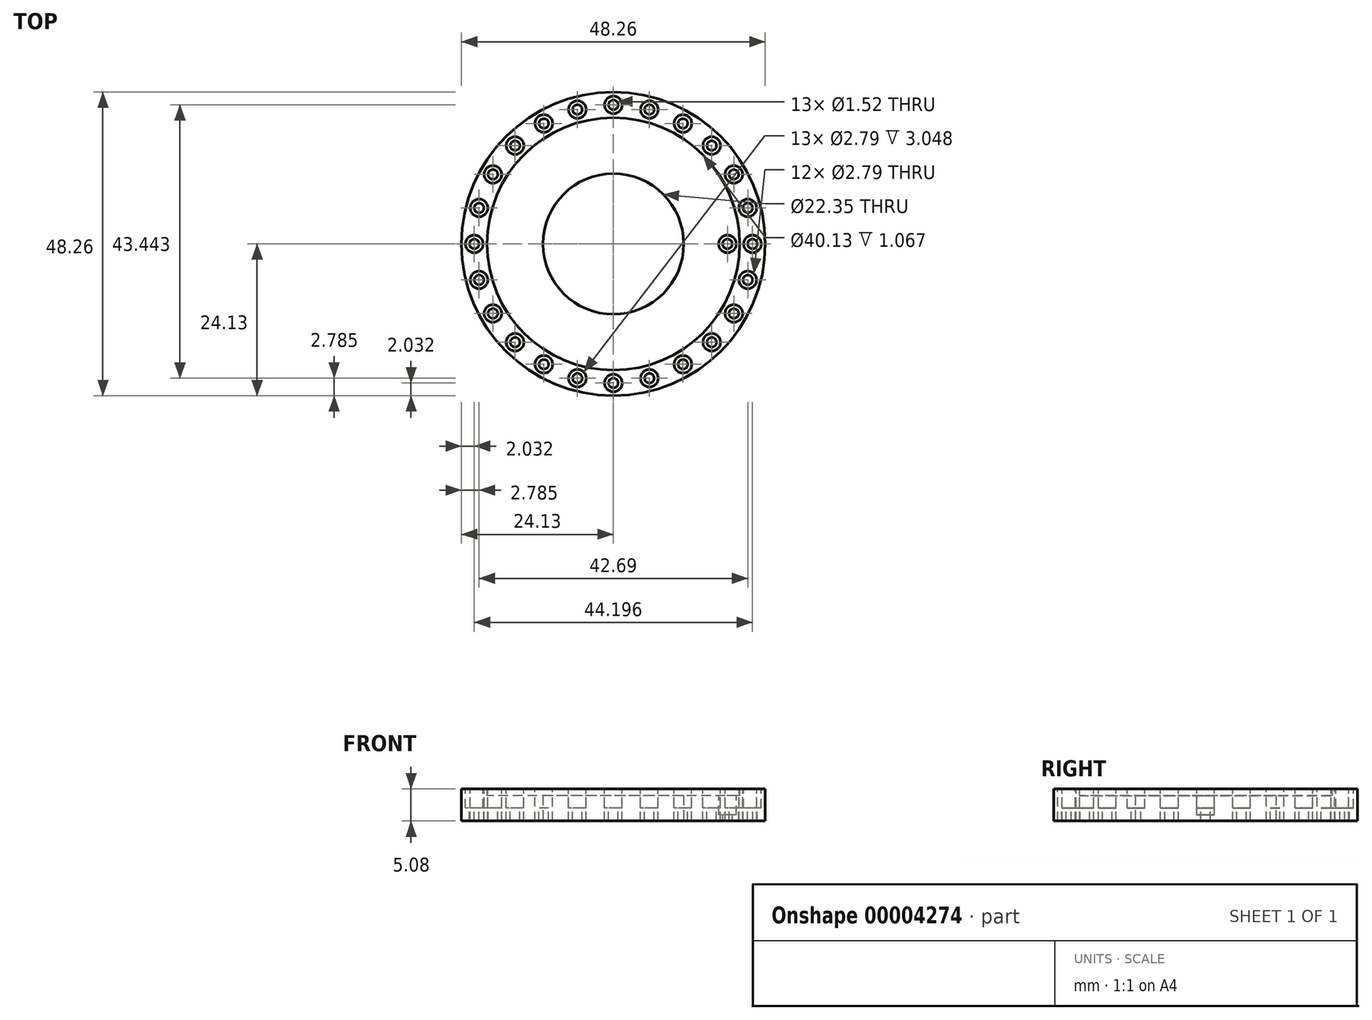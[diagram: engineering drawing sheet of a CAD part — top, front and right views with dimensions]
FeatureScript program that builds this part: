
annotation { "Feature Type Name" : "Feature", "Feature Type Description" : "" }
export const myFeature = defineFeature(function(context is Context, id is Id, definition is map)
    precondition{}
    {
        {
            var Q0;
            Q0=qCreatedBy(makeId("Top.planeOp"),FACE);
            var sketch = newSketch(context, id + "F0", { "sketchPlane" : qUnion([Q0])});
            skCircle(sketch, "E0", {"center": v(0, 0) * mm, "radius": 24.13 * mm});
            skCircle(sketch, "E1", {"center": v(0, 0) * mm, "radius": 20.07 * mm});
            skCircle(sketch, "E2", {"center": v(0, 0) * mm, "radius": 11.18 * mm});
            skSolve(sketch);
        }
        {
            var Q0;
            Q0=makeQuery(id+"F0.imprint","IMPRINT",FACE,{"disambiguationData":[TD([[makeQuery(id+"F0.imprint","IMPRINT",EDGE,{"derivedFrom":sQuery(id+"F0.wireOp",EDGE,"E1")}),1.0]])]});
            extrude(context, id + "F1", {"entities" : qUnion([Q0]), "depth" : 4 * mm});
        }
        {
            var Q0;
            Q0=makeQuery(id+"F0.imprint","IMPRINT",FACE,{"disambiguationData":[TD([[makeQuery(id+"F0.imprint","IMPRINT",EDGE,{"derivedFrom":sQuery(id+"F0.wireOp",EDGE,"E0")}),1.0]])]});
            extrude(context, id + "F2", {"entities" : qUnion([Q0]), "operationType" : NewBodyOperationType.ADD, "depth" : 5.08 * mm});
        }
        {
            var Q0;
            Q0=makeQuery(id+"F1.opExtrude","CAP_FACE",FACE,{"disambiguationData":[OSD([sQuery(id+"F0.wireOp",EDGE,"E1"),sQuery(id+"F0.wireOp",EDGE,"E2")])],"isStart":false});
            var sketch = newSketch(context, id + "F3", { "sketchPlane" : qUnion([Q0])});
            skLineSegment(sketch, "E3", {"start": v(0, 0) * mm, "end": v(16.71, 0) * mm});
            skCircle(sketch, "E4", {"center": v(18.11, 0) * mm, "radius": 0.76 * mm});
            skLineSegment(sketch, "E5.trimOffspring", {"start": v(19.5, 0) * mm, "end": v(20.07, 0) * mm});
            skCircle(sketch, "E6", {"center": v(18.11, 0) * mm, "radius": 1.4 * mm});
            skSolve(sketch);
        }
        {
            var Q0;
            {var subQ0=sQuery(id+"F3.wireOp",EDGE,"E4");var subQ2=makeQuery(id+"F3.imprint","INTERSECT",VERTEX,{"derivedFrom":[sQuery(id+"F3.wireOp",EDGE,"E3"),subQ0]});Q0=makeQuery(id+"F3.imprint","IMPRINT",FACE,{"disambiguationData":[TD([[makeQuery(id+"F3.imprint","IMPRINT",EDGE,{"disambiguationData":[TD([[subQ2,1.0]])],"derivedFrom":subQ0}),1.0]])]});}
            extrude(context, id + "F4", {"entities" : qUnion([Q0]), "operationType" : NewBodyOperationType.REMOVE, "endBound" : BoundingType.THROUGH_ALL, "oppositeDirection" : true, "depth" : 2.8 * mm});
        }
        {
            var Q0;
            Q0=makeQuery(id+"F2.opExtrude","CAP_FACE",FACE,{"disambiguationData":[OSD([sQuery(id+"F0.wireOp",EDGE,"E0"),sQuery(id+"F0.wireOp",EDGE,"E1")])],"isStart":false});
            var sketch = newSketch(context, id + "F5", { "sketchPlane" : qUnion([Q0])});
            skLineSegment(sketch, "E7", {"start": v(0, 0) * mm, "end": v(21.34, 0) * mm, "construction": true});
            skLineSegment(sketch, "E8", {"start": v(0, 0) * mm, "end": v(20.6, 5.52) * mm, "construction": true});
            skCircle(sketch, "E9", {"center": v(22.1, 0) * mm, "radius": 0.76 * mm});
            skCircle(sketch, "E10", {"center": v(21.35, 5.72) * mm, "radius": 0.76 * mm});
            skCircle(sketch, "E11.0.MirrorC", {"center": v(19.14, 11.05) * mm, "radius": 0.76 * mm});
            skLineSegment(sketch, "E12", {"start": v(0, 0) * mm, "end": v(18.48, 10.67) * mm, "construction": true});
            skCircle(sketch, "E13.0.MirrorC", {"center": v(15.63, 15.63) * mm, "radius": 0.76 * mm});
            skCircle(sketch, "E14.0.MirrorC", {"center": v(11.05, 19.14) * mm, "radius": 0.76 * mm});
            skLineSegment(sketch, "E15", {"start": v(0, 0) * mm, "end": v(10.67, 18.48) * mm, "construction": true});
            skCircle(sketch, "E16.0.MirrorC", {"center": v(5.72, 21.35) * mm, "radius": 0.76 * mm});
            skCircle(sketch, "E17.0.MirrorC", {"center": v(0, 22.1) * mm, "radius": 0.76 * mm});
            skCircle(sketch, "E18.0.MirrorC", {"center": v(-5.72, 21.35) * mm, "radius": 0.76 * mm});
            skCircle(sketch, "E19.0.MirrorC", {"center": v(-11.05, 19.14) * mm, "radius": 0.76 * mm});
            skLineSegment(sketch, "E20", {"start": v(0, 0) * mm, "end": v(-10.67, 18.48) * mm, "construction": true});
            skCircle(sketch, "E21.0.MirrorC", {"center": v(-15.63, 15.63) * mm, "radius": 0.76 * mm});
            skCircle(sketch, "E22.0.MirrorC", {"center": v(-19.14, 11.05) * mm, "radius": 0.76 * mm});
            skCircle(sketch, "E23.0.MirrorC", {"center": v(-21.35, 5.72) * mm, "radius": 0.76 * mm});
            skCircle(sketch, "E24.0.MirrorC", {"center": v(-22.1, 0) * mm, "radius": 0.76 * mm});
            skCircle(sketch, "E25.0.MirrorC", {"center": v(-21.35, -5.72) * mm, "radius": 0.76 * mm});
            skCircle(sketch, "E26.0.MirrorC", {"center": v(-19.14, -11.05) * mm, "radius": 0.76 * mm});
            skCircle(sketch, "E27.0.MirrorC", {"center": v(-15.63, -15.63) * mm, "radius": 0.76 * mm});
            skCircle(sketch, "E28.0.MirrorC", {"center": v(-11.05, -19.14) * mm, "radius": 0.76 * mm});
            skCircle(sketch, "E29.0.MirrorC", {"center": v(21.35, -5.72) * mm, "radius": 0.76 * mm});
            skCircle(sketch, "E30.0.MirrorC", {"center": v(19.14, -11.05) * mm, "radius": 0.76 * mm});
            skCircle(sketch, "E31.0.MirrorC", {"center": v(15.63, -15.63) * mm, "radius": 0.76 * mm});
            skCircle(sketch, "E32.0.MirrorC", {"center": v(11.05, -19.14) * mm, "radius": 0.76 * mm});
            skCircle(sketch, "E33.0.MirrorC", {"center": v(5.72, -21.35) * mm, "radius": 0.76 * mm});
            skCircle(sketch, "E34.0.MirrorC", {"center": v(0, -22.1) * mm, "radius": 0.76 * mm});
            skCircle(sketch, "E35.0.MirrorC", {"center": v(-5.72, -21.35) * mm, "radius": 0.76 * mm});
            skLineSegment(sketch, "E36.trimOffspring", {"start": v(22.08, 5.92) * mm, "end": v(23.3, 6.25) * mm, "construction": true});
            skLineSegment(sketch, "E37.trimOffspring", {"start": v(22.86, 0) * mm, "end": v(24.13, 0) * mm, "construction": true});
            skCircle(sketch, "E38", {"center": v(22.1, 0) * mm, "radius": 1.4 * mm});
            skCircle(sketch, "E39", {"center": v(21.35, 5.72) * mm, "radius": 1.4 * mm});
            skCircle(sketch, "E40", {"center": v(19.14, 11.05) * mm, "radius": 1.4 * mm});
            skCircle(sketch, "E41", {"center": v(15.63, 15.63) * mm, "radius": 1.4 * mm});
            skCircle(sketch, "E42", {"center": v(11.05, 19.14) * mm, "radius": 1.4 * mm});
            skCircle(sketch, "E43", {"center": v(5.72, 21.35) * mm, "radius": 1.4 * mm});
            skCircle(sketch, "E44", {"center": v(0, 22.1) * mm, "radius": 1.4 * mm});
            skCircle(sketch, "E45", {"center": v(-5.72, 21.35) * mm, "radius": 1.4 * mm});
            skCircle(sketch, "E46", {"center": v(-11.05, 19.14) * mm, "radius": 1.4 * mm});
            skCircle(sketch, "E47", {"center": v(-15.63, 15.63) * mm, "radius": 1.4 * mm});
            skCircle(sketch, "E48", {"center": v(-19.14, 11.05) * mm, "radius": 1.4 * mm});
            skCircle(sketch, "E49", {"center": v(-21.35, 5.72) * mm, "radius": 1.4 * mm});
            skCircle(sketch, "E50", {"center": v(-22.1, 0) * mm, "radius": 1.4 * mm});
            skCircle(sketch, "E51", {"center": v(-21.35, -5.72) * mm, "radius": 1.4 * mm});
            skCircle(sketch, "E52", {"center": v(-19.14, -11.05) * mm, "radius": 1.4 * mm});
            skCircle(sketch, "E53", {"center": v(-15.63, -15.63) * mm, "radius": 1.4 * mm});
            skCircle(sketch, "E54", {"center": v(-11.05, -19.14) * mm, "radius": 1.4 * mm});
            skCircle(sketch, "E55", {"center": v(-5.72, -21.35) * mm, "radius": 1.4 * mm});
            skCircle(sketch, "E56", {"center": v(0, -22.1) * mm, "radius": 1.4 * mm});
            skCircle(sketch, "E57", {"center": v(5.72, -21.35) * mm, "radius": 1.4 * mm});
            skCircle(sketch, "E58", {"center": v(11.05, -19.14) * mm, "radius": 1.4 * mm});
            skCircle(sketch, "E59", {"center": v(15.63, -15.63) * mm, "radius": 1.4 * mm});
            skCircle(sketch, "E60", {"center": v(19.14, -11.05) * mm, "radius": 1.4 * mm});
            skCircle(sketch, "E61", {"center": v(21.35, -5.72) * mm, "radius": 1.4 * mm});
            skSolve(sketch);
        }
        {
            var Q0;
            Q0=makeQuery(id+"F5.imprint","IMPRINT",FACE,{"disambiguationData":[TD([[makeQuery(id+"F5.imprint","IMPRINT",EDGE,{"derivedFrom":sQuery(id+"F5.wireOp",EDGE,"E9")}),1.0]])]});
            var Q1;
            Q1=makeQuery(id+"F5.imprint","IMPRINT",FACE,{"disambiguationData":[TD([[makeQuery(id+"F5.imprint","IMPRINT",EDGE,{"derivedFrom":sQuery(id+"F5.wireOp",EDGE,"E10")}),1.0]])]});
            var Q2;
            Q2=makeQuery(id+"F5.imprint","IMPRINT",FACE,{"disambiguationData":[TD([[makeQuery(id+"F5.imprint","IMPRINT",EDGE,{"derivedFrom":sQuery(id+"F5.wireOp",EDGE,"E11.0.MirrorC")}),-1.0]])]});
            var Q3;
            Q3=makeQuery(id+"F5.imprint","IMPRINT",FACE,{"disambiguationData":[TD([[makeQuery(id+"F5.imprint","IMPRINT",EDGE,{"derivedFrom":sQuery(id+"F5.wireOp",EDGE,"E13.0.MirrorC")}),-1.0]])]});
            var Q4;
            Q4=makeQuery(id+"F5.imprint","IMPRINT",FACE,{"disambiguationData":[TD([[makeQuery(id+"F5.imprint","IMPRINT",EDGE,{"derivedFrom":sQuery(id+"F5.wireOp",EDGE,"E14.0.MirrorC")}),-1.0]])]});
            var Q5;
            Q5=makeQuery(id+"F5.imprint","IMPRINT",FACE,{"disambiguationData":[TD([[makeQuery(id+"F5.imprint","IMPRINT",EDGE,{"derivedFrom":sQuery(id+"F5.wireOp",EDGE,"E16.0.MirrorC")}),1.0]])]});
            var Q6;
            Q6=makeQuery(id+"F5.imprint","IMPRINT",FACE,{"disambiguationData":[TD([[makeQuery(id+"F5.imprint","IMPRINT",EDGE,{"derivedFrom":sQuery(id+"F5.wireOp",EDGE,"E17.0.MirrorC")}),1.0]])]});
            var Q7;
            Q7=makeQuery(id+"F5.imprint","IMPRINT",FACE,{"disambiguationData":[TD([[makeQuery(id+"F5.imprint","IMPRINT",EDGE,{"derivedFrom":sQuery(id+"F5.wireOp",EDGE,"E18.0.MirrorC")}),-1.0]])]});
            var Q8;
            Q8=makeQuery(id+"F5.imprint","IMPRINT",FACE,{"disambiguationData":[TD([[makeQuery(id+"F5.imprint","IMPRINT",EDGE,{"derivedFrom":sQuery(id+"F5.wireOp",EDGE,"E19.0.MirrorC")}),-1.0]])]});
            var Q9;
            Q9=makeQuery(id+"F5.imprint","IMPRINT",FACE,{"disambiguationData":[TD([[makeQuery(id+"F5.imprint","IMPRINT",EDGE,{"derivedFrom":sQuery(id+"F5.wireOp",EDGE,"E21.0.MirrorC")}),1.0]])]});
            var Q10;
            Q10=makeQuery(id+"F5.imprint","IMPRINT",FACE,{"disambiguationData":[TD([[makeQuery(id+"F5.imprint","IMPRINT",EDGE,{"derivedFrom":sQuery(id+"F5.wireOp",EDGE,"E22.0.MirrorC")}),-1.0]])]});
            var Q11;
            Q11=makeQuery(id+"F5.imprint","IMPRINT",FACE,{"disambiguationData":[TD([[makeQuery(id+"F5.imprint","IMPRINT",EDGE,{"derivedFrom":sQuery(id+"F5.wireOp",EDGE,"E23.0.MirrorC")}),-1.0]])]});
            var Q12;
            Q12=makeQuery(id+"F5.imprint","IMPRINT",FACE,{"disambiguationData":[TD([[makeQuery(id+"F5.imprint","IMPRINT",EDGE,{"derivedFrom":sQuery(id+"F5.wireOp",EDGE,"E24.0.MirrorC")}),1.0]])]});
            var Q13;
            Q13=makeQuery(id+"F5.imprint","IMPRINT",FACE,{"disambiguationData":[TD([[makeQuery(id+"F5.imprint","IMPRINT",EDGE,{"derivedFrom":sQuery(id+"F5.wireOp",EDGE,"E25.0.MirrorC")}),1.0]])]});
            var Q14;
            Q14=makeQuery(id+"F5.imprint","IMPRINT",FACE,{"disambiguationData":[TD([[makeQuery(id+"F5.imprint","IMPRINT",EDGE,{"derivedFrom":sQuery(id+"F5.wireOp",EDGE,"E26.0.MirrorC")}),1.0]])]});
            var Q15;
            Q15=makeQuery(id+"F5.imprint","IMPRINT",FACE,{"disambiguationData":[TD([[makeQuery(id+"F5.imprint","IMPRINT",EDGE,{"derivedFrom":sQuery(id+"F5.wireOp",EDGE,"E27.0.MirrorC")}),-1.0]])]});
            var Q16;
            Q16=makeQuery(id+"F5.imprint","IMPRINT",FACE,{"disambiguationData":[TD([[makeQuery(id+"F5.imprint","IMPRINT",EDGE,{"derivedFrom":sQuery(id+"F5.wireOp",EDGE,"E28.0.MirrorC")}),-1.0]])]});
            var Q17;
            Q17=makeQuery(id+"F5.imprint","IMPRINT",FACE,{"disambiguationData":[TD([[makeQuery(id+"F5.imprint","IMPRINT",EDGE,{"derivedFrom":sQuery(id+"F5.wireOp",EDGE,"E35.0.MirrorC")}),1.0]])]});
            var Q18;
            Q18=makeQuery(id+"F5.imprint","IMPRINT",FACE,{"disambiguationData":[TD([[makeQuery(id+"F5.imprint","IMPRINT",EDGE,{"derivedFrom":sQuery(id+"F5.wireOp",EDGE,"E34.0.MirrorC")}),-1.0]])]});
            var Q19;
            Q19=makeQuery(id+"F5.imprint","IMPRINT",FACE,{"disambiguationData":[TD([[makeQuery(id+"F5.imprint","IMPRINT",EDGE,{"derivedFrom":sQuery(id+"F5.wireOp",EDGE,"E33.0.MirrorC")}),-1.0]])]});
            var Q20;
            Q20=makeQuery(id+"F5.imprint","IMPRINT",FACE,{"disambiguationData":[TD([[makeQuery(id+"F5.imprint","IMPRINT",EDGE,{"derivedFrom":sQuery(id+"F5.wireOp",EDGE,"E32.0.MirrorC")}),1.0]])]});
            var Q21;
            Q21=makeQuery(id+"F5.imprint","IMPRINT",FACE,{"disambiguationData":[TD([[makeQuery(id+"F5.imprint","IMPRINT",EDGE,{"derivedFrom":sQuery(id+"F5.wireOp",EDGE,"E31.0.MirrorC")}),1.0]])]});
            var Q22;
            Q22=makeQuery(id+"F5.imprint","IMPRINT",FACE,{"disambiguationData":[TD([[makeQuery(id+"F5.imprint","IMPRINT",EDGE,{"derivedFrom":sQuery(id+"F5.wireOp",EDGE,"E30.0.MirrorC")}),1.0]])]});
            var Q23;
            Q23=makeQuery(id+"F5.imprint","IMPRINT",FACE,{"disambiguationData":[TD([[makeQuery(id+"F5.imprint","IMPRINT",EDGE,{"derivedFrom":sQuery(id+"F5.wireOp",EDGE,"E29.0.MirrorC")}),-1.0]])]});
            extrude(context, id + "F6", {"entities" : qUnion([Q0, Q1, Q2, Q3, Q4, Q5, Q6, Q7, Q8, Q9, Q10, Q11, Q12, Q13, Q14, Q15, Q16, Q17, Q18, Q19, Q20, Q21, Q22, Q23]), "operationType" : NewBodyOperationType.REMOVE, "endBound" : BoundingType.THROUGH_ALL, "oppositeDirection" : true, "depth" : 2.8 * mm});
        }
        {
            var Q0;
            Q0 = qSketchRegion(id + "F3", true);
            extrude(context, id + "F7", {"entities" : qUnion([Q0]), "operationType" : NewBodyOperationType.REMOVE, "oppositeDirection" : true, "depth" : 3.05 * mm});
        }
        {
            var Q0;
            Q0=makeQuery(id+"F5.imprint","IMPRINT",FACE,{"disambiguationData":[TD([[makeQuery(id+"F5.imprint","IMPRINT",EDGE,{"derivedFrom":sQuery(id+"F5.wireOp",EDGE,"E9")}),-1.0]])]});
            var Q1;
            Q1=makeQuery(id+"F5.imprint","IMPRINT",FACE,{"disambiguationData":[TD([[makeQuery(id+"F5.imprint","IMPRINT",EDGE,{"derivedFrom":sQuery(id+"F5.wireOp",EDGE,"E10")}),-1.0]])]});
            var Q2;
            Q2=makeQuery(id+"F5.imprint","IMPRINT",FACE,{"disambiguationData":[TD([[makeQuery(id+"F5.imprint","IMPRINT",EDGE,{"derivedFrom":sQuery(id+"F5.wireOp",EDGE,"E29.0.MirrorC")}),1.0]])]});
            var Q3;
            Q3=makeQuery(id+"F5.imprint","IMPRINT",FACE,{"disambiguationData":[TD([[makeQuery(id+"F5.imprint","IMPRINT",EDGE,{"derivedFrom":sQuery(id+"F5.wireOp",EDGE,"E11.0.MirrorC")}),1.0]])]});
            var Q4;
            Q4=makeQuery(id+"F5.imprint","IMPRINT",FACE,{"disambiguationData":[TD([[makeQuery(id+"F5.imprint","IMPRINT",EDGE,{"derivedFrom":sQuery(id+"F5.wireOp",EDGE,"E13.0.MirrorC")}),1.0]])]});
            var Q5;
            Q5=makeQuery(id+"F5.imprint","IMPRINT",FACE,{"disambiguationData":[TD([[makeQuery(id+"F5.imprint","IMPRINT",EDGE,{"derivedFrom":sQuery(id+"F5.wireOp",EDGE,"E14.0.MirrorC")}),1.0]])]});
            var Q6;
            Q6=makeQuery(id+"F5.imprint","IMPRINT",FACE,{"disambiguationData":[TD([[makeQuery(id+"F5.imprint","IMPRINT",EDGE,{"derivedFrom":sQuery(id+"F5.wireOp",EDGE,"E16.0.MirrorC")}),-1.0]])]});
            var Q7;
            Q7=makeQuery(id+"F5.imprint","IMPRINT",FACE,{"disambiguationData":[TD([[makeQuery(id+"F5.imprint","IMPRINT",EDGE,{"derivedFrom":sQuery(id+"F5.wireOp",EDGE,"E17.0.MirrorC")}),-1.0]])]});
            var Q8;
            Q8=makeQuery(id+"F5.imprint","IMPRINT",FACE,{"disambiguationData":[TD([[makeQuery(id+"F5.imprint","IMPRINT",EDGE,{"derivedFrom":sQuery(id+"F5.wireOp",EDGE,"E18.0.MirrorC")}),1.0]])]});
            var Q9;
            Q9=makeQuery(id+"F5.imprint","IMPRINT",FACE,{"disambiguationData":[TD([[makeQuery(id+"F5.imprint","IMPRINT",EDGE,{"derivedFrom":sQuery(id+"F5.wireOp",EDGE,"E19.0.MirrorC")}),1.0]])]});
            var Q10;
            Q10=makeQuery(id+"F5.imprint","IMPRINT",FACE,{"disambiguationData":[TD([[makeQuery(id+"F5.imprint","IMPRINT",EDGE,{"derivedFrom":sQuery(id+"F5.wireOp",EDGE,"E21.0.MirrorC")}),-1.0]])]});
            var Q11;
            Q11=makeQuery(id+"F5.imprint","IMPRINT",FACE,{"disambiguationData":[TD([[makeQuery(id+"F5.imprint","IMPRINT",EDGE,{"derivedFrom":sQuery(id+"F5.wireOp",EDGE,"E22.0.MirrorC")}),1.0]])]});
            var Q12;
            Q12=makeQuery(id+"F5.imprint","IMPRINT",FACE,{"disambiguationData":[TD([[makeQuery(id+"F5.imprint","IMPRINT",EDGE,{"derivedFrom":sQuery(id+"F5.wireOp",EDGE,"E23.0.MirrorC")}),1.0]])]});
            var Q13;
            Q13=makeQuery(id+"F5.imprint","IMPRINT",FACE,{"disambiguationData":[TD([[makeQuery(id+"F5.imprint","IMPRINT",EDGE,{"derivedFrom":sQuery(id+"F5.wireOp",EDGE,"E24.0.MirrorC")}),-1.0]])]});
            var Q14;
            Q14=makeQuery(id+"F5.imprint","IMPRINT",FACE,{"disambiguationData":[TD([[makeQuery(id+"F5.imprint","IMPRINT",EDGE,{"derivedFrom":sQuery(id+"F5.wireOp",EDGE,"E25.0.MirrorC")}),-1.0]])]});
            var Q15;
            Q15=makeQuery(id+"F5.imprint","IMPRINT",FACE,{"disambiguationData":[TD([[makeQuery(id+"F5.imprint","IMPRINT",EDGE,{"derivedFrom":sQuery(id+"F5.wireOp",EDGE,"E26.0.MirrorC")}),-1.0]])]});
            var Q16;
            Q16=makeQuery(id+"F5.imprint","IMPRINT",FACE,{"disambiguationData":[TD([[makeQuery(id+"F5.imprint","IMPRINT",EDGE,{"derivedFrom":sQuery(id+"F5.wireOp",EDGE,"E27.0.MirrorC")}),1.0]])]});
            var Q17;
            Q17=makeQuery(id+"F5.imprint","IMPRINT",FACE,{"disambiguationData":[TD([[makeQuery(id+"F5.imprint","IMPRINT",EDGE,{"derivedFrom":sQuery(id+"F5.wireOp",EDGE,"E28.0.MirrorC")}),1.0]])]});
            var Q18;
            Q18=makeQuery(id+"F5.imprint","IMPRINT",FACE,{"disambiguationData":[TD([[makeQuery(id+"F5.imprint","IMPRINT",EDGE,{"derivedFrom":sQuery(id+"F5.wireOp",EDGE,"E35.0.MirrorC")}),-1.0]])]});
            var Q19;
            Q19=makeQuery(id+"F5.imprint","IMPRINT",FACE,{"disambiguationData":[TD([[makeQuery(id+"F5.imprint","IMPRINT",EDGE,{"derivedFrom":sQuery(id+"F5.wireOp",EDGE,"E34.0.MirrorC")}),1.0]])]});
            var Q20;
            Q20=makeQuery(id+"F5.imprint","IMPRINT",FACE,{"disambiguationData":[TD([[makeQuery(id+"F5.imprint","IMPRINT",EDGE,{"derivedFrom":sQuery(id+"F5.wireOp",EDGE,"E33.0.MirrorC")}),1.0]])]});
            var Q21;
            Q21=makeQuery(id+"F5.imprint","IMPRINT",FACE,{"disambiguationData":[TD([[makeQuery(id+"F5.imprint","IMPRINT",EDGE,{"derivedFrom":sQuery(id+"F5.wireOp",EDGE,"E32.0.MirrorC")}),-1.0]])]});
            var Q22;
            Q22=makeQuery(id+"F5.imprint","IMPRINT",FACE,{"disambiguationData":[TD([[makeQuery(id+"F5.imprint","IMPRINT",EDGE,{"derivedFrom":sQuery(id+"F5.wireOp",EDGE,"E31.0.MirrorC")}),-1.0]])]});
            var Q23;
            Q23=makeQuery(id+"F5.imprint","IMPRINT",FACE,{"disambiguationData":[TD([[makeQuery(id+"F5.imprint","IMPRINT",EDGE,{"derivedFrom":sQuery(id+"F5.wireOp",EDGE,"E30.0.MirrorC")}),-1.0]])]});
            extrude(context, id + "F8", {"entities" : qUnion([Q0, Q1, Q2, Q3, Q4, Q5, Q6, Q7, Q8, Q9, Q10, Q11, Q12, Q13, Q14, Q15, Q16, Q17, Q18, Q19, Q20, Q21, Q22, Q23]), "operationType" : NewBodyOperationType.REMOVE, "oppositeDirection" : true, "depth" : 3.05 * mm});
        }
    });
